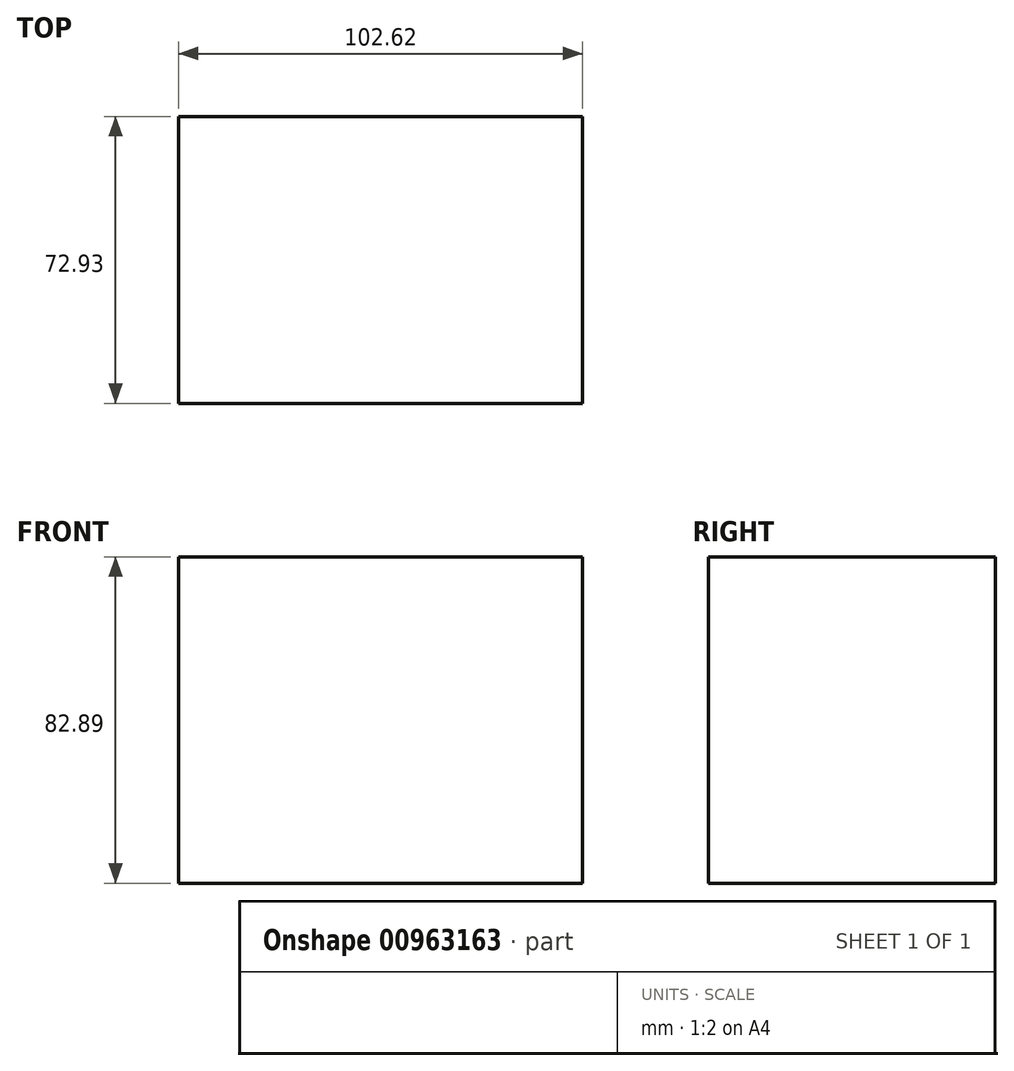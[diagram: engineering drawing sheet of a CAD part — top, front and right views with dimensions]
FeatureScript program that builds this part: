
annotation { "Feature Type Name" : "Feature", "Feature Type Description" : "" }
export const myFeature = defineFeature(function(context is Context, id is Id, definition is map)
    precondition{}
    {
        {
            var Q0;
            Q0=qCreatedBy(makeId("Front.planeOp"),FACE);
            var sketch = newSketch(context, id + "F0", { "sketchPlane" : qUnion([Q0])});
            skLineSegment(sketch, "E0.bottom", {"start": v(-49.66, 37.12) * mm, "end": v(52.96, 37.12) * mm});
            skLineSegment(sketch, "E0.top", {"start": v(-49.66, -45.77) * mm, "end": v(52.96, -45.77) * mm});
            skLineSegment(sketch, "E0.left", {"start": v(-49.66, 37.12) * mm, "end": v(-49.66, -45.77) * mm});
            skLineSegment(sketch, "E0.right", {"start": v(52.96, 37.12) * mm, "end": v(52.96, -45.77) * mm});
            skSolve(sketch);
        }
        {
            var Q0;
            Q0=makeQuery(id+"F0.imprint","IMPRINT",FACE,{"disambiguationData":[TD([[makeQuery(id+"F0.imprint","IMPRINT",EDGE,{"derivedFrom":sQuery(id+"F0.wireOp",EDGE,"E0.bottom")}),-1.0]])]});
            cPlane(context, id + "F1", {"entities" : qUnion([Q0]), "cplaneType" : CPlaneType.OFFSET, "offset" : 72.93 * mm, "width" : 152.4 * mm, "height" : 152.4 * mm});
        }
        {
            var Q0;
            Q0=qCreatedBy(id+"F1.planeOp",FACE);
            var sketch = newSketch(context, id + "F2", { "sketchPlane" : qUnion([Q0])});
            skLineSegment(sketch, "E1.bottom", {"start": v(-49.66, 37.12) * mm, "end": v(52.96, 37.12) * mm});
            skLineSegment(sketch, "E1.top", {"start": v(-49.66, -45.77) * mm, "end": v(52.96, -45.77) * mm});
            skLineSegment(sketch, "E1.left", {"start": v(-49.66, 37.12) * mm, "end": v(-49.66, -45.77) * mm});
            skLineSegment(sketch, "E1.right", {"start": v(52.96, 37.12) * mm, "end": v(52.96, -45.77) * mm});
            skSolve(sketch);
        }
        {
            var Q0;
            Q0=makeQuery(id+"F0.imprint","IMPRINT",FACE,{"disambiguationData":[TD([[makeQuery(id+"F0.imprint","IMPRINT",EDGE,{"derivedFrom":sQuery(id+"F0.wireOp",EDGE,"E0.bottom")}),-1.0]])]});
            var Q1;
            Q1=makeQuery(id+"F2.imprint","IMPRINT",FACE,{"disambiguationData":[TD([[makeQuery(id+"F2.imprint","IMPRINT",EDGE,{"derivedFrom":sQuery(id+"F2.wireOp",EDGE,"E1.bottom")}),-1.0]])]});
            loft(context, id + "F3", {"sheetProfilesArray" : [{ "sheetProfileEntities" : qUnion([Q0]) }, { "sheetProfileEntities" : qUnion([Q1]) }]});
        }
    });
